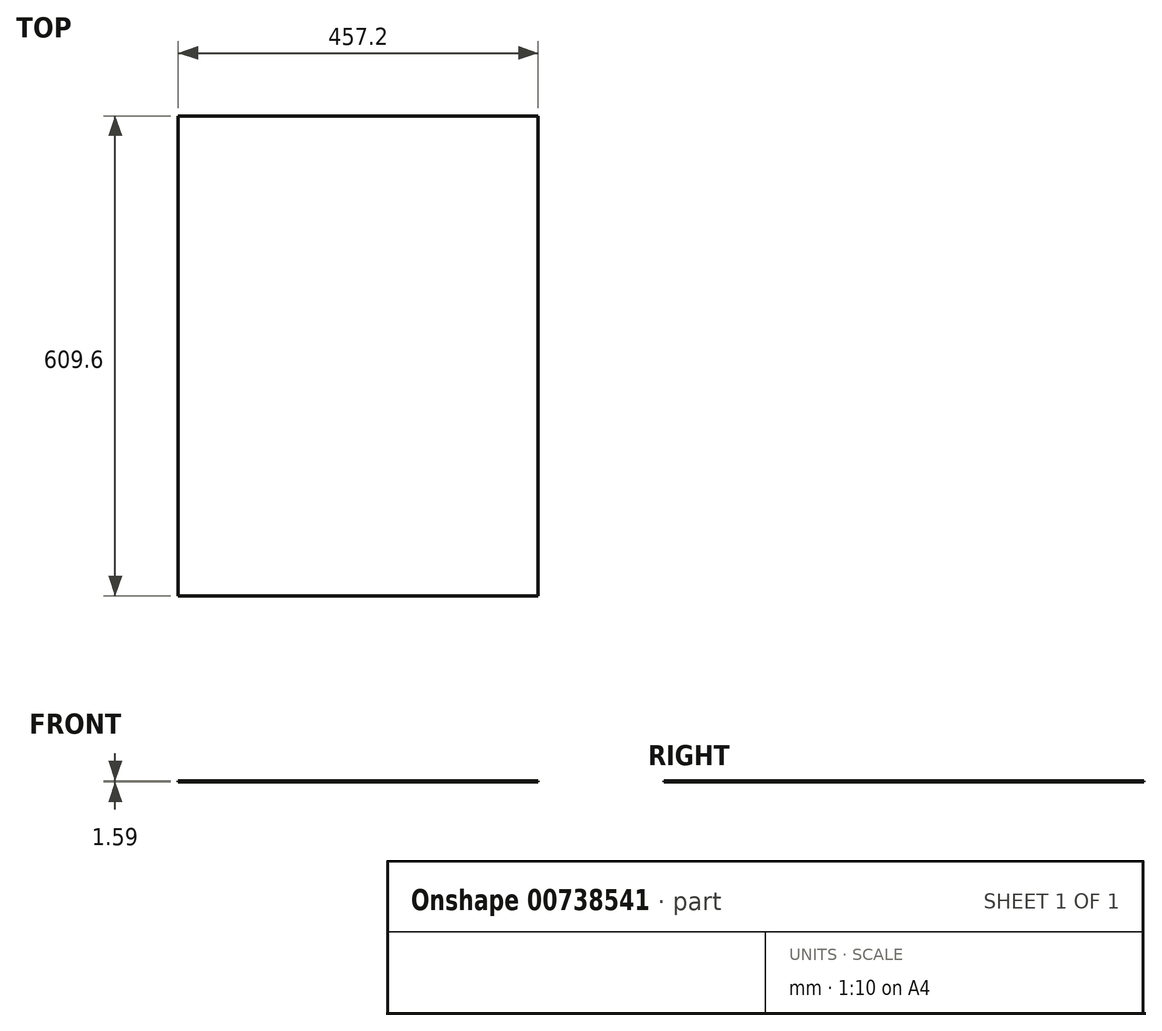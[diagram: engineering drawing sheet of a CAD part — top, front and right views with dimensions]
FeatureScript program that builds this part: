
annotation { "Feature Type Name" : "Feature", "Feature Type Description" : "" }
export const myFeature = defineFeature(function(context is Context, id is Id, definition is map)
    precondition{}
    {
        {
            var Q0;
            Q0=qCreatedBy(makeId("Top.planeOp"),FACE);
            var sketch = newSketch(context, id + "F0", { "sketchPlane" : qUnion([Q0])});
            skLineSegment(sketch, "E0.bottom", {"start": v(0, 0) * mm, "end": v(457.2, 0) * mm});
            skLineSegment(sketch, "E0.top", {"start": v(0, -609.6) * mm, "end": v(457.2, -609.6) * mm});
            skLineSegment(sketch, "E0.left", {"start": v(0, 0) * mm, "end": v(0, -609.6) * mm});
            skLineSegment(sketch, "E0.right", {"start": v(457.2, 0) * mm, "end": v(457.2, -609.6) * mm});
            skSolve(sketch);
        }
        {
            var Q0;
            Q0 = qSketchRegion(id + "F0", true);
            extrude(context, id + "F1", {"entities" : qUnion([Q0]), "depth" : 1.59 * mm, "offsetDistance" : 25.4 * mm});
        }
    });
